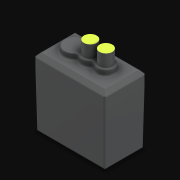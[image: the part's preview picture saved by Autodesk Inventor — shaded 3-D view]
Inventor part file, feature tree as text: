
AUTODESK INVENTOR PART (.ipt)
format: ipt  version: 2021 (Build 250183000, 183)  size: 302,592 bytes
history: native  units: in
note: dims shown in document units (in); Inventor stores cm internally (conversion verified against a paired STEP export)
features: chamfer x6, extrude x3, sketch x3, fillet x2
ambient origin geometry x8: Origin, YZ Plane, XZ Plane, XY Plane, X Axis, Y Axis, Z Axis, Center Point
bodies: Solid1 (feature_tree)
feature tree (14):
  extrude  "Extrusion1"  Depth=2.82in
  extrude  "Extrusion2"  Depth=0.125in
  chamfer  "Chamfer1"  Distance=0.592in
  chamfer  "Chamfer2"  Distance=0.125in
  chamfer  "Chamfer3"  Distance=0.125in
  chamfer  "Chamfer4"  Distance=0.125in
  chamfer  "Chamfer5"  Distance=0.125in
  chamfer  "Chamfer6"  Distance=0.125in
  extrude  "Extrusion4"  Depth=0.0625in
  fillet  "Fillet1"  Radius=0.53in
  fillet  "Fillet2"  Radius=0.658in
  sketch  "Sketch1"  dims[d0=2.257in d1=2.82in]
  sketch  "Sketch3"  dims[d2=1.3in d3=0.0in d12=0.52in d20=0.592in d21=0.0in d30=0.12in d31=0.125in d32=0.2749in d33=0.12in d34=0.125in d35=0.3436in d36=1.641in d37=0.125in d38=0.0069in d39=1.641in d40=0.125in d41=0.0069in d42=1.641in d43=0.125in d44=0.0069in]
  sketch  "Sketch5"  dims[d45=1.641in d46=0.125in d47=0.0069in d48=0.53in d49=0.53in d50=0.658in d52=0.406in d54=0.406in d55=0.5in d56=0.189in d57=0.0in d58=0.125in d59=0.0625in d60=0.0312in d61=0.0625in d66=0.0in d67=0.0in]
